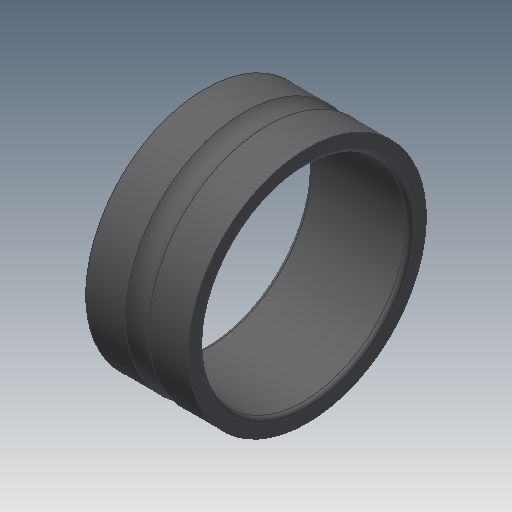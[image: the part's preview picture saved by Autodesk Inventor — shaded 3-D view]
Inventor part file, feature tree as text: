
AUTODESK INVENTOR PART (.ipt)
format: ipt  version: 2019.4 (Build 234330000, 330)  size: 207,872 bytes
history: native  units: mm
features: other x133, revolve x1, sketch x1
ambient origin geometry x8: Origin, YZ Plane, XZ Plane, XY Plane, X Axis, Y Axis, Z Axis, Center Point
bodies: Solid1 (feature_tree)
feature tree (135):
  revolve  "Revolution1"  [1 undecoded]
  other  "ip_st_1_1_XY"
  other  "ip_st_1_1_YZ"
  other  "ip_st_1_1_ZX"
  other  "ip_st_1_1_X"
  other  "ip_st_1_1_Y"
  other  "ip_st_1_1_Z"
  other  "ip_st_1_1_Center"
  other  "ip_st_1_10_XY"
  other  "ip_st_1_10_YZ"
  other  "ip_st_1_10_ZX"
  other  "ip_st_1_10_X"
  other  "ip_st_1_10_Y"
  other  "ip_st_1_10_Z"
  other  "ip_st_1_10_Center"
  other  "ip_st_1_11_XY"
  other  "ip_st_1_11_YZ"
  other  "ip_st_1_11_ZX"
  other  "ip_st_1_11_X"
  other  "ip_st_1_11_Y"
  other  "ip_st_1_11_Z"
  other  "ip_st_1_11_Center"
  other  "ip_st_1_12_XY"
  other  "ip_st_1_12_YZ"
  other  "ip_st_1_12_ZX"
  other  "ip_st_1_12_X"
  other  "ip_st_1_12_Y"
  other  "ip_st_1_12_Z"
  other  "ip_st_1_12_Center"
  other  "ip_st_1_13_XY"
  other  "ip_st_1_13_YZ"
  other  "ip_st_1_13_ZX"
  other  "ip_st_1_13_X"
  other  "ip_st_1_13_Y"
  other  "ip_st_1_13_Z"
  other  "ip_st_1_13_Center"
  other  "ip_st_1_14_XY"
  other  "ip_st_1_14_YZ"
  other  "ip_st_1_14_ZX"
  other  "ip_st_1_14_X"
  other  "ip_st_1_14_Y"
  other  "ip_st_1_14_Z"
  other  "ip_st_1_14_Center"
  other  "ip_st_1_15_XY"
  other  "ip_st_1_15_YZ"
  other  "ip_st_1_15_ZX"
  other  "ip_st_1_15_X"
  other  "ip_st_1_15_Y"
  other  "ip_st_1_15_Z"
  other  "ip_st_1_15_Center"
  other  "ip_st_1_16_XY"
  other  "ip_st_1_16_YZ"
  other  "ip_st_1_16_ZX"
  other  "ip_st_1_16_X"
  other  "ip_st_1_16_Y"
  other  "ip_st_1_16_Z"
  other  "ip_st_1_16_Center"
  other  "ip_st_1_17_XY"
  other  "ip_st_1_17_YZ"
  other  "ip_st_1_17_ZX"
  other  "ip_st_1_17_X"
  other  "ip_st_1_17_Y"
  other  "ip_st_1_17_Z"
  other  "ip_st_1_17_Center"
  other  "ip_st_1_2_XY"
  other  "ip_st_1_2_YZ"
  other  "ip_st_1_2_ZX"
  other  "ip_st_1_2_X"
  other  "ip_st_1_2_Y"
  other  "ip_st_1_2_Z"
  other  "ip_st_1_2_Center"
  other  "ip_st_1_3_XY"
  other  "ip_st_1_3_YZ"
  other  "ip_st_1_3_ZX"
  other  "ip_st_1_3_X"
  other  "ip_st_1_3_Y"
  other  "ip_st_1_3_Z"
  other  "ip_st_1_3_Center"
  other  "ip_st_1_4_XY"
  other  "ip_st_1_4_YZ"
  other  "ip_st_1_4_ZX"
  other  "ip_st_1_4_X"
  other  "ip_st_1_4_Y"
  other  "ip_st_1_4_Z"
  other  "ip_st_1_4_Center"
  other  "ip_st_1_5_XY"
  other  "ip_st_1_5_YZ"
  other  "ip_st_1_5_ZX"
  other  "ip_st_1_5_X"
  other  "ip_st_1_5_Y"
  other  "ip_st_1_5_Z"
  other  "ip_st_1_5_Center"
  other  "ip_st_1_6_XY"
  other  "ip_st_1_6_YZ"
  other  "ip_st_1_6_ZX"
  other  "ip_st_1_6_X"
  other  "ip_st_1_6_Y"
  other  "ip_st_1_6_Z"
  other  "ip_st_1_6_Center"
  other  "ip_st_1_7_XY"
  other  "ip_st_1_7_YZ"
  other  "ip_st_1_7_ZX"
  other  "ip_st_1_7_X"
  other  "ip_st_1_7_Y"
  other  "ip_st_1_7_Z"
  other  "ip_st_1_7_Center"
  other  "ip_st_1_8_XY"
  other  "ip_st_1_8_YZ"
  other  "ip_st_1_8_ZX"
  other  "ip_st_1_8_X"
  other  "ip_st_1_8_Y"
  other  "ip_st_1_8_Z"
  other  "ip_st_1_8_Center"
  other  "ip_st_1_9_XY"
  other  "ip_st_1_9_YZ"
  other  "ip_st_1_9_ZX"
  other  "ip_st_1_9_X"
  other  "ip_st_1_9_Y"
  other  "ip_st_1_9_Z"
  other  "ip_st_1_9_Center"
  other  "ip_st_1a_XY"
  other  "ip_st_1a_YZ"
  other  "ip_st_1a_ZX"
  other  "ip_st_1a_X"
  other  "ip_st_1a_Y"
  other  "ip_st_1a_Z"
  other  "ip_st_1a_Center"
  other  "ip_st_2a_XY"
  other  "ip_st_2a_YZ"
  other  "ip_st_2a_ZX"
  other  "ip_st_2a_X"
  other  "ip_st_2a_Y"
  other  "ip_st_2a_Z"
  other  "ip_st_2a_Center"
  sketch  "Sketch_1"  dims[d0=360.0deg d1=0.0mm]
note: 1 required parameter value undecoded (feature->parameter linkage not recoverable at this tier; creation-order binding heuristic only, values carry confidence <= 0.55)
